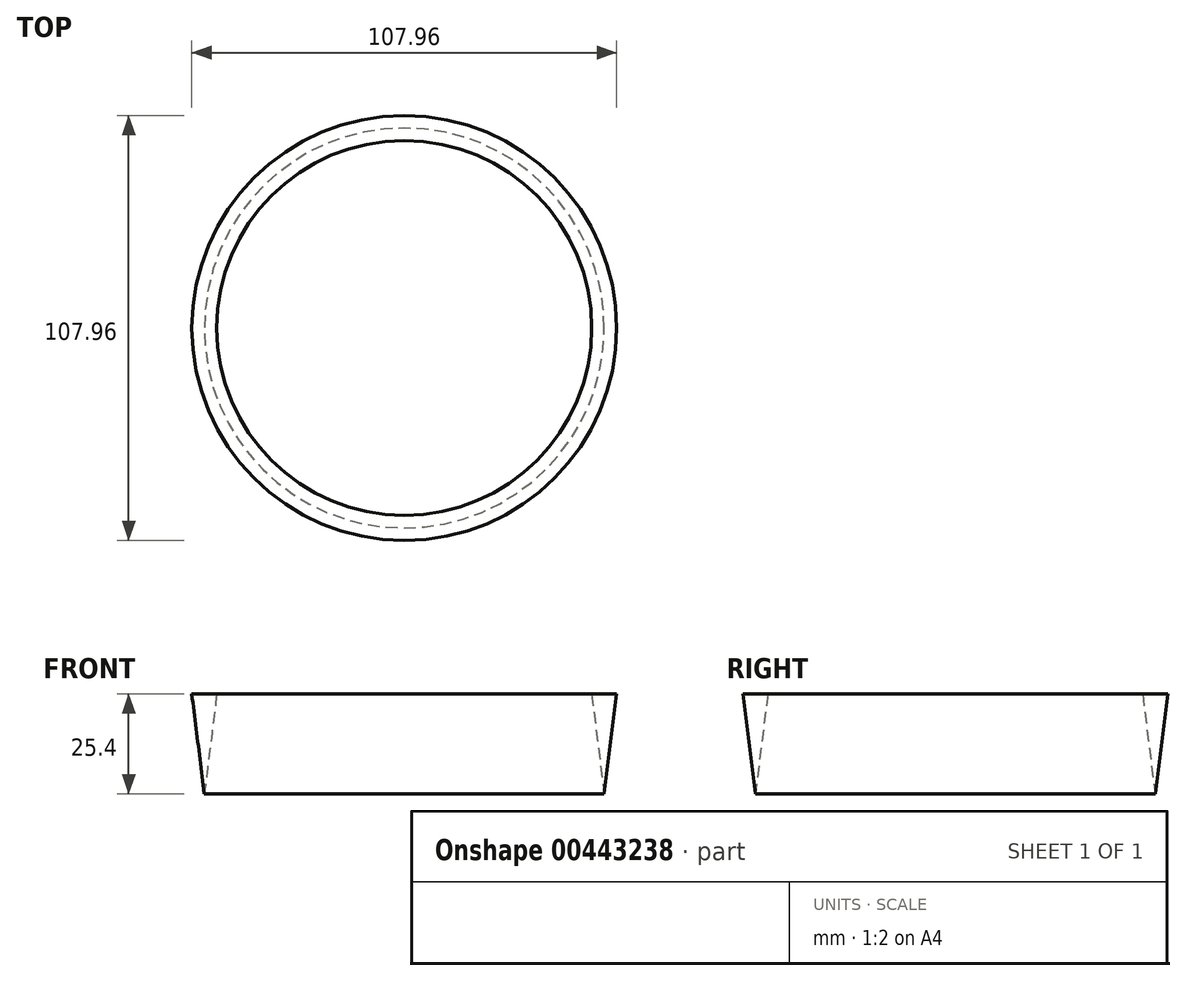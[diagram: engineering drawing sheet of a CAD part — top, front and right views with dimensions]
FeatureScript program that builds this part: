
annotation { "Feature Type Name" : "Feature", "Feature Type Description" : "" }
export const myFeature = defineFeature(function(context is Context, id is Id, definition is map)
    precondition{}
    {
        {
            var Q0;
            Q0=qCreatedBy(makeId("Top.planeOp"),FACE);
            var sketch = newSketch(context, id + "F0", { "sketchPlane" : qUnion([Q0])});
            skCircle(sketch, "E0", {"center": v(0, 0) * mm, "radius": 50.8 * mm});
            skSolve(sketch);
        }
        {
            var Q0;
            Q0=qCreatedBy(makeId("Front.planeOp"),FACE);
            var sketch = newSketch(context, id + "F1", { "sketchPlane" : qUnion([Q0])});
            skLineSegment(sketch, "E1", {"start": v(-50.8, 0) * mm, "end": v(-50.8, 25.4) * mm, "construction": true});
            skLineSegment(sketch, "E2", {"start": v(-50.8, 0) * mm, "end": v(-53.98, 25.4) * mm});
            skLineSegment(sketch, "E3", {"start": v(-53.98, 25.4) * mm, "end": v(-47.63, 25.4) * mm});
            skLineSegment(sketch, "E4", {"start": v(-47.62, 25.4) * mm, "end": v(-50.8, 0) * mm});
            skSolve(sketch);
        }
        {
            var Q0;
            Q0=qCreatedBy(makeId("Front.planeOp"),FACE);
            var sketch = newSketch(context, id + "F2", { "sketchPlane" : qUnion([Q0])});
            skLineSegment(sketch, "E5", {"start": v(0, 0) * mm, "end": v(0, 21.37) * mm});
            skSolve(sketch);
        }
        {
            var Q0;
            Q0=makeQuery(id+"F1.imprint","IMPRINT",FACE,{"disambiguationData":[TD([[makeQuery(id+"F1.imprint","IMPRINT",EDGE,{"derivedFrom":sQuery(id+"F1.wireOp",EDGE,"E2")}),-1.0]])]});
            var Q1;
            Q1=sQuery(id+"F2.wireOp",EDGE,"E5");
            revolve(context, id + "F3", {"entities" : qUnion([Q0]), "axis" : qUnion([Q1]), "revolveType" : RevolveType.FULL});
        }
    });
